FCSTD DOCUMENT  (FreeCAD 1.0R39109 (Git))
Label: Frame
License: All rights reserved
LicenseURL: http://en.wikipedia.org/wiki/All_rights_reserved
objects: Spreadsheet::Sheet×1, App::Link×1
EXTERNAL_REF file=Frame_Shape_H.FCStd obj=Part
EXTERNAL_REF file=Frame_Shape_Star.FCStd obj=Part
EXTERNAL_REF file=Frame_Shape_T.FCStd obj=Part
EXTERNAL_REF file=../../Master_of_Puppets.FCStd obj=Alternator
EXTERNAL_REF file=../../Master_of_Puppets.FCStd obj=Spreadsheet

FEATURE [Spreadsheet::Sheet] Spreadsheet
  cells = A1='Inputs; A2='CalculatedWindTurbineShape; B2(CalculatedWindTurbineShape)==Master_of_Puppets#Spreadsheet.CalculatedWindTurbineShape; A3='Frame; A4='TShapeFrame; B4(TShapeFramePart)==<<Frame_Shape_T>>#Part._self; A5='HShapeFrame; B5(HShapeFramePart)==<<Frame_Shape_H>>#Part._self; A6='StarShapeFrame; B6(StarShapeFramePart)==<<Frame_Shape_Star>>#Part._self; A7='Frame; B7(FramePart)==CalculatedWindTurbineShape == <<T>> ? TShapeFramePart : (CalculatedWindTurbineShape == <<H>> ? HShapeFramePart : StarShapeFramePart); A8='Frame Y; A9='TShapeFrameY; B9(TShapeFrameY)==Master_of_Puppets#Alternator.BC - Master_of_Puppets#Alternator.X; A10='HShapeFrameY; B10(HShapeFrameY)==Master_of_Puppets#Alternator.HH / 2; A11='StarShapeFrameY; B11(StarShapeFrameY)==Master_of_Puppets#Alternator.B / 2; A12='FrameY; B12(FrameY)==CalculatedWindTurbineShape == <<T>> ? TShapeFrameY : (CalculatedWindTurbineShape == <<H>> ? HShapeFrameY : StarShapeFrameY)
FEATURE [App::Link] Link  label="Frame"
  LinkPlacement = pos=(0,167.5,0) rot=(0,0.707107,-0.707107;3.14159rad)
  LinkedObject = -> <external Frame_Shape_T.FCStd>#Part
  Placement = pos=(0,167.5,0) rot=(0,0.707107,-0.707107;3.14159rad)
  expr: .Placement.Base.y = Spreadsheet.FrameY
  expr: LinkedObject = Spreadsheet.FramePart
